# Revit family: Faucet-Lavatory-KOHLER-Hone-K-22535IN
name_source: partatom
category: Plumbing Fixtures
revit_build: Autodesk Revit 2017 (Build: 20160225_1515(x64)
units: mm (PartAtom-declared; Revit-internal decimal feet)

## family parameters
Cut with Voids When Loaded = No
Host = Face
OmniClass Number = 23.31.11.00
OmniClass Title = Faucets
Part Type = Normal
Room Calculation Point = No
Round Connector Dimension = Use Diameter
Shared = No

## types (4) — shared parameters
ADA Compliant = No
Assembly Code = D2010
CW Connection = Yes
Cold Water Inlet = Cold Water Inlet
Date Modified = 10/13/2020
Default Elevation = 36"
Faucet Hole Spacing = 0"
Flow Rate = 0 GPM
HW Connection = Yes
Handle Clearance = 3 7/16"
Height = 10 9/16"
Hot Water Inlet = Hot Water Inlet
Length = 4 3/4"
Manufacturer = KOHLER Co.
Master Format 2014 = 22 41 39
Master Format 2014 Name = Residential Faucets, Supplies, and Trim
Material = Premium Metal Construction
Pressure = 0.00 psi
Product Name = Hone
Product Page URL = https://www.kohler.co.in
Spout Reach = 4 3/4"
URL = https://www.kohler.co.in
Vent Connection = No
Waste Connection = No
Waste Water Outlet = Waste Water Outlet
WaterSense Certified = No
Width = 1 13/16"

## per-type parameters (varying)
| type | Description | Drain Included | Finish | Lift Rod | Model | Type |
| CP-Polished Chrome | HONE SC Tall FAUCET With DRAIN | Yes | Kohler-Metal-CP-Polished_Chrome | Yes | K-22535IN-4-CP | 1 |
| Without drain,CP-Polished Chrome | HONE SC Tall LAV FAUCET Without drain | No | Kohler-Metal-AF-Flange_Gold | No | K-22535IN-4ND-CP | 2 |
| Without drain,AF-Flange Gold | HONE SC Tall LAV FAUCET Without drain | No | Kohler-Metal-AF-Flange_Gold | No | K-22535IN-4ND-AF | 3 |
| Without drain,BN-Roman Silver | HONE SC Tall LAV FAUCET Without drain | No | Kohler-Metal-BN-Roman_Silver | No | K-22535IN-4ND-BN | 4 |

## geometry (parser evidence)
native form markers: Sweep x5
no freeform markers — native parametric forms only
